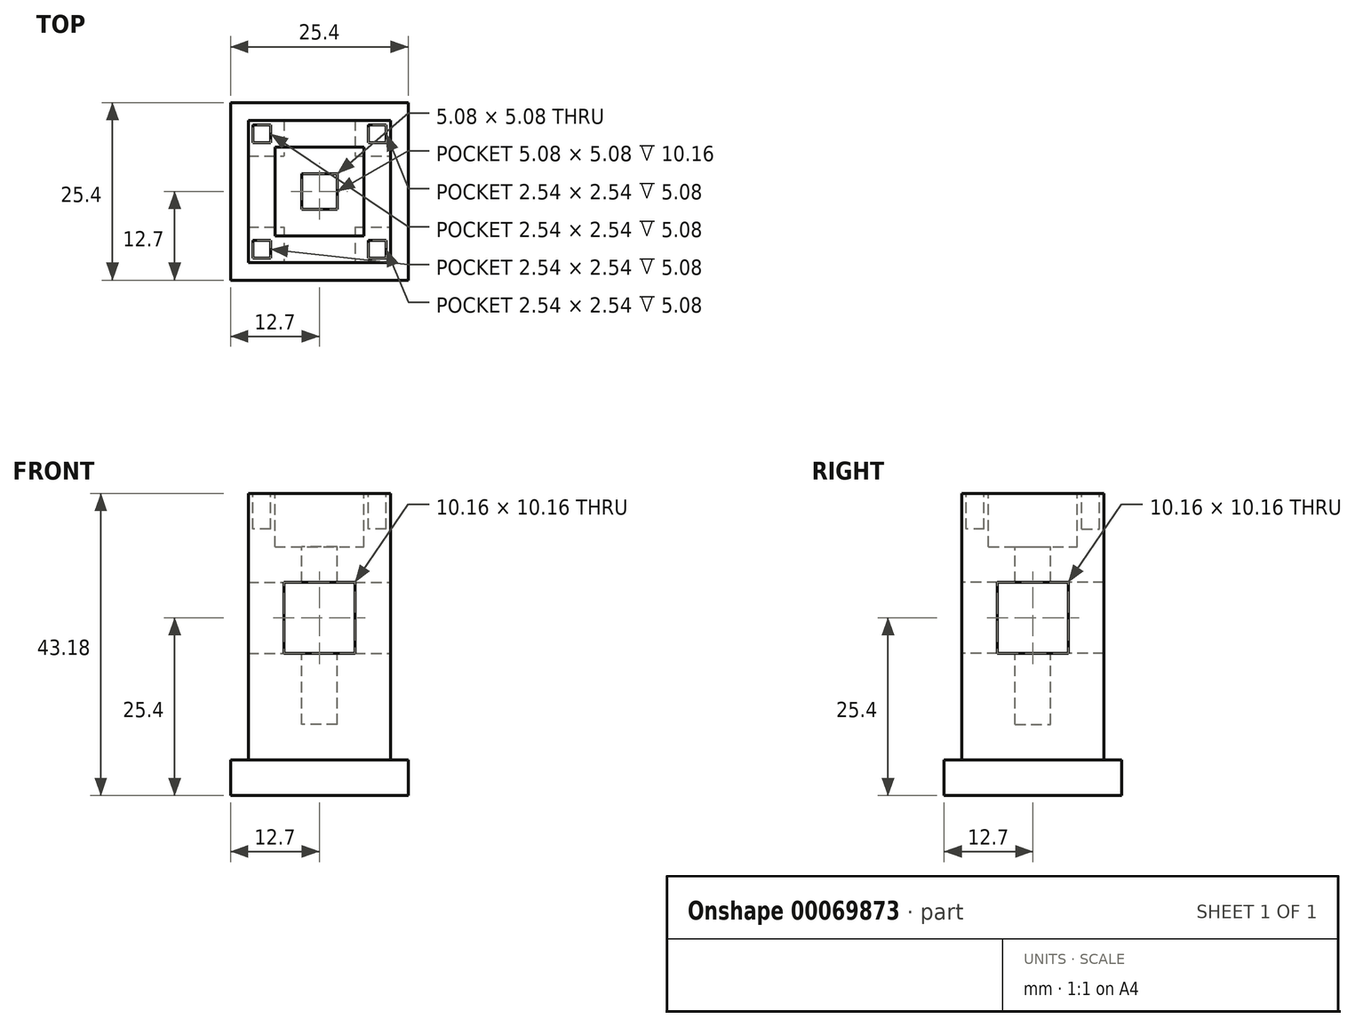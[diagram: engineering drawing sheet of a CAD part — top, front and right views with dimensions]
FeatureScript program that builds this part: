
annotation { "Feature Type Name" : "Feature", "Feature Type Description" : "" }
export const myFeature = defineFeature(function(context is Context, id is Id, definition is map)
    precondition{}
    {
        {
            var Q0;
            Q0=qCreatedBy(makeId("Top.planeOp"),FACE);
            var sketch = newSketch(context, id + "F0", { "sketchPlane" : qUnion([Q0])});
            skLineSegment(sketch, "E0.bottom", {"start": v(0, 0) * mm, "end": v(25.4, 0) * mm});
            skLineSegment(sketch, "E0.top", {"start": v(0, -25.4) * mm, "end": v(25.4, -25.4) * mm});
            skLineSegment(sketch, "E0.left", {"start": v(0, 0) * mm, "end": v(0, -25.4) * mm});
            skLineSegment(sketch, "E0.right", {"start": v(25.4, 0) * mm, "end": v(25.4, -25.4) * mm});
            skSolve(sketch);
        }
        {
            var Q0;
            Q0 = qSketchRegion(id + "F0", true);
            extrude(context, id + "F1", {"entities" : qUnion([Q0]), "depth" : 5.08 * mm});
        }
        {
            var Q0;
            Q0=makeQuery(id+"F1.opExtrude","CAP_FACE",FACE,{"disambiguationData":[OSD([sQuery(id+"F0.wireOp",EDGE,"E0.bottom"),sQuery(id+"F0.wireOp",EDGE,"E0.top"),sQuery(id+"F0.wireOp",EDGE,"E0.left"),sQuery(id+"F0.wireOp",EDGE,"E0.right")])],"isStart":false});
            var sketch = newSketch(context, id + "F2", { "sketchPlane" : qUnion([Q0])});
            skLineSegment(sketch, "E1.bottom", {"start": v(2.54, -2.54) * mm, "end": v(22.86, -2.54) * mm});
            skLineSegment(sketch, "E1.top", {"start": v(2.54, -22.86) * mm, "end": v(22.86, -22.86) * mm});
            skLineSegment(sketch, "E1.left", {"start": v(2.54, -2.54) * mm, "end": v(2.54, -22.86) * mm});
            skLineSegment(sketch, "E1.right", {"start": v(22.86, -2.54) * mm, "end": v(22.86, -22.86) * mm});
            skSolve(sketch);
        }
        {
            var Q0;
            Q0 = qSketchRegion(id + "F2", true);
            extrude(context, id + "F3", {"entities" : qUnion([Q0]), "operationType" : NewBodyOperationType.ADD, "depth" : 38.1 * mm});
        }
        {
            var Q0;
            Q0=makeQuery(id+"F3.opExtrude","CAP_FACE",FACE,{"disambiguationData":[OSD([sQuery(id+"F2.wireOp",EDGE,"E1.bottom"),sQuery(id+"F2.wireOp",EDGE,"E1.top"),sQuery(id+"F2.wireOp",EDGE,"E1.left"),sQuery(id+"F2.wireOp",EDGE,"E1.right")])],"isStart":false});
            var sketch = newSketch(context, id + "F4", { "sketchPlane" : qUnion([Q0])});
            skLineSegment(sketch, "E2.bottom", {"start": v(6.35, -19.05) * mm, "end": v(19.05, -19.05) * mm});
            skLineSegment(sketch, "E2.top", {"start": v(6.35, -6.35) * mm, "end": v(19.05, -6.35) * mm});
            skLineSegment(sketch, "E2.left", {"start": v(6.35, -19.05) * mm, "end": v(6.35, -6.35) * mm});
            skLineSegment(sketch, "E2.right", {"start": v(19.05, -19.05) * mm, "end": v(19.05, -6.35) * mm});
            skSolve(sketch);
        }
        {
            var Q0;
            Q0 = qSketchRegion(id + "F4", true);
            extrude(context, id + "F5", {"entities" : qUnion([Q0]), "operationType" : NewBodyOperationType.REMOVE, "oppositeDirection" : true, "depth" : 7.62 * mm});
        }
        {
            var Q0;
            Q0=makeQuery(id+"F3.opExtrude","SWEPT_FACE",FACE,{"disambiguationData":[OSD([sQuery(id+"F2.wireOp",EDGE,"E1.right")])]});
            var sketch = newSketch(context, id + "F6", { "sketchPlane" : qUnion([Q0])});
            skLineSegment(sketch, "E3.bottom", {"start": v(-17.78, 30.48) * mm, "end": v(-7.62, 30.48) * mm});
            skLineSegment(sketch, "E3.top", {"start": v(-17.78, 20.32) * mm, "end": v(-7.62, 20.32) * mm});
            skLineSegment(sketch, "E3.left", {"start": v(-17.78, 30.48) * mm, "end": v(-17.78, 20.32) * mm});
            skLineSegment(sketch, "E3.right", {"start": v(-7.62, 30.48) * mm, "end": v(-7.62, 20.32) * mm});
            skSolve(sketch);
        }
        {
            var Q0;
            Q0 = qSketchRegion(id + "F6", true);
            extrude(context, id + "F7", {"entities" : qUnion([Q0]), "operationType" : NewBodyOperationType.REMOVE, "oppositeDirection" : true, "depth" : 25.4 * mm});
        }
        {
            var Q0;
            Q0=makeQuery(id+"F5.boolean.opBoolean","COPY",FACE,{"derivedFrom":makeQuery(id+"F5.opExtrude","CAP_FACE",FACE,{"disambiguationData":[OSD([sQuery(id+"F4.wireOp",EDGE,"E2.bottom"),sQuery(id+"F4.wireOp",EDGE,"E2.top"),sQuery(id+"F4.wireOp",EDGE,"E2.left"),sQuery(id+"F4.wireOp",EDGE,"E2.right")])],"isStart":false})});
            var sketch = newSketch(context, id + "F8", { "sketchPlane" : qUnion([Q0])});
            skLineSegment(sketch, "E4.bottom", {"start": v(15.24, -15.24) * mm, "end": v(10.16, -15.24) * mm});
            skLineSegment(sketch, "E4.top", {"start": v(15.24, -10.16) * mm, "end": v(10.16, -10.16) * mm});
            skLineSegment(sketch, "E4.left", {"start": v(15.24, -15.24) * mm, "end": v(15.24, -10.16) * mm});
            skLineSegment(sketch, "E4.right", {"start": v(10.16, -15.24) * mm, "end": v(10.16, -10.16) * mm});
            skSolve(sketch);
        }
        {
            var Q0;
            Q0 = qSketchRegion(id + "F8", true);
            extrude(context, id + "F9", {"entities" : qUnion([Q0]), "operationType" : NewBodyOperationType.REMOVE, "oppositeDirection" : true, "depth" : 25.4 * mm});
        }
        {
            var Q0;
            Q0=makeQuery(id+"F3.opExtrude","SWEPT_FACE",FACE,{"disambiguationData":[OSD([sQuery(id+"F2.wireOp",EDGE,"E1.top")])]});
            var sketch = newSketch(context, id + "F10", { "sketchPlane" : qUnion([Q0])});
            skLineSegment(sketch, "E5.bottom", {"start": v(7.62, 30.48) * mm, "end": v(17.78, 30.48) * mm});
            skLineSegment(sketch, "E5.top", {"start": v(7.62, 20.32) * mm, "end": v(17.78, 20.32) * mm});
            skLineSegment(sketch, "E5.left", {"start": v(7.62, 30.48) * mm, "end": v(7.62, 20.32) * mm});
            skLineSegment(sketch, "E5.right", {"start": v(17.78, 30.48) * mm, "end": v(17.78, 20.32) * mm});
            skSolve(sketch);
        }
        {
            var Q0;
            Q0 = qSketchRegion(id + "F10", true);
            extrude(context, id + "F11", {"entities" : qUnion([Q0]), "operationType" : NewBodyOperationType.REMOVE, "oppositeDirection" : true, "depth" : 25.4 * mm});
        }
        {
            var Q0;
            Q0=makeQuery(id+"F3.opExtrude","CAP_FACE",FACE,{"disambiguationData":[OSD([sQuery(id+"F2.wireOp",EDGE,"E1.bottom"),sQuery(id+"F2.wireOp",EDGE,"E1.top"),sQuery(id+"F2.wireOp",EDGE,"E1.left"),sQuery(id+"F2.wireOp",EDGE,"E1.right")])],"isStart":false});
            var sketch = newSketch(context, id + "F12", { "sketchPlane" : qUnion([Q0])});
            skLineSegment(sketch, "E6.top", {"start": v(22.23, -3.17) * mm, "end": v(19.69, -3.17) * mm});
            skLineSegment(sketch, "E6.left", {"start": v(22.23, -5.71) * mm, "end": v(22.23, -3.17) * mm});
            skLineSegment(sketch, "E6.right", {"start": v(19.69, -5.71) * mm, "end": v(19.69, -3.17) * mm});
            skLineSegment(sketch, "E7", {"start": v(19.69, -5.71) * mm, "end": v(22.23, -5.71) * mm});
            skLineSegment(sketch, "E8.bottom", {"start": v(5.72, -5.71) * mm, "end": v(3.18, -5.71) * mm});
            skLineSegment(sketch, "E8.top", {"start": v(5.72, -3.17) * mm, "end": v(3.18, -3.17) * mm});
            skLineSegment(sketch, "E8.left", {"start": v(5.72, -5.71) * mm, "end": v(5.72, -3.17) * mm});
            skLineSegment(sketch, "E8.right", {"start": v(3.17, -5.71) * mm, "end": v(3.17, -3.17) * mm});
            skLineSegment(sketch, "E9.bottom", {"start": v(5.72, -19.69) * mm, "end": v(3.18, -19.69) * mm});
            skLineSegment(sketch, "E9.top", {"start": v(5.72, -22.23) * mm, "end": v(3.18, -22.23) * mm});
            skLineSegment(sketch, "E9.left", {"start": v(5.72, -19.69) * mm, "end": v(5.72, -22.23) * mm});
            skLineSegment(sketch, "E9.right", {"start": v(3.18, -19.69) * mm, "end": v(3.18, -22.23) * mm});
            skLineSegment(sketch, "E10.bottom", {"start": v(19.69, -19.69) * mm, "end": v(22.23, -19.69) * mm});
            skLineSegment(sketch, "E10.top", {"start": v(19.69, -22.23) * mm, "end": v(22.23, -22.23) * mm});
            skLineSegment(sketch, "E10.left", {"start": v(19.69, -19.69) * mm, "end": v(19.69, -22.23) * mm});
            skLineSegment(sketch, "E10.right", {"start": v(22.23, -19.69) * mm, "end": v(22.23, -22.23) * mm});
            skSolve(sketch);
        }
        {
            var Q0;
            Q0 = qSketchRegion(id + "F12", true);
            extrude(context, id + "F13", {"entities" : qUnion([Q0]), "operationType" : NewBodyOperationType.REMOVE, "oppositeDirection" : true, "depth" : 5.08 * mm});
        }
    });
